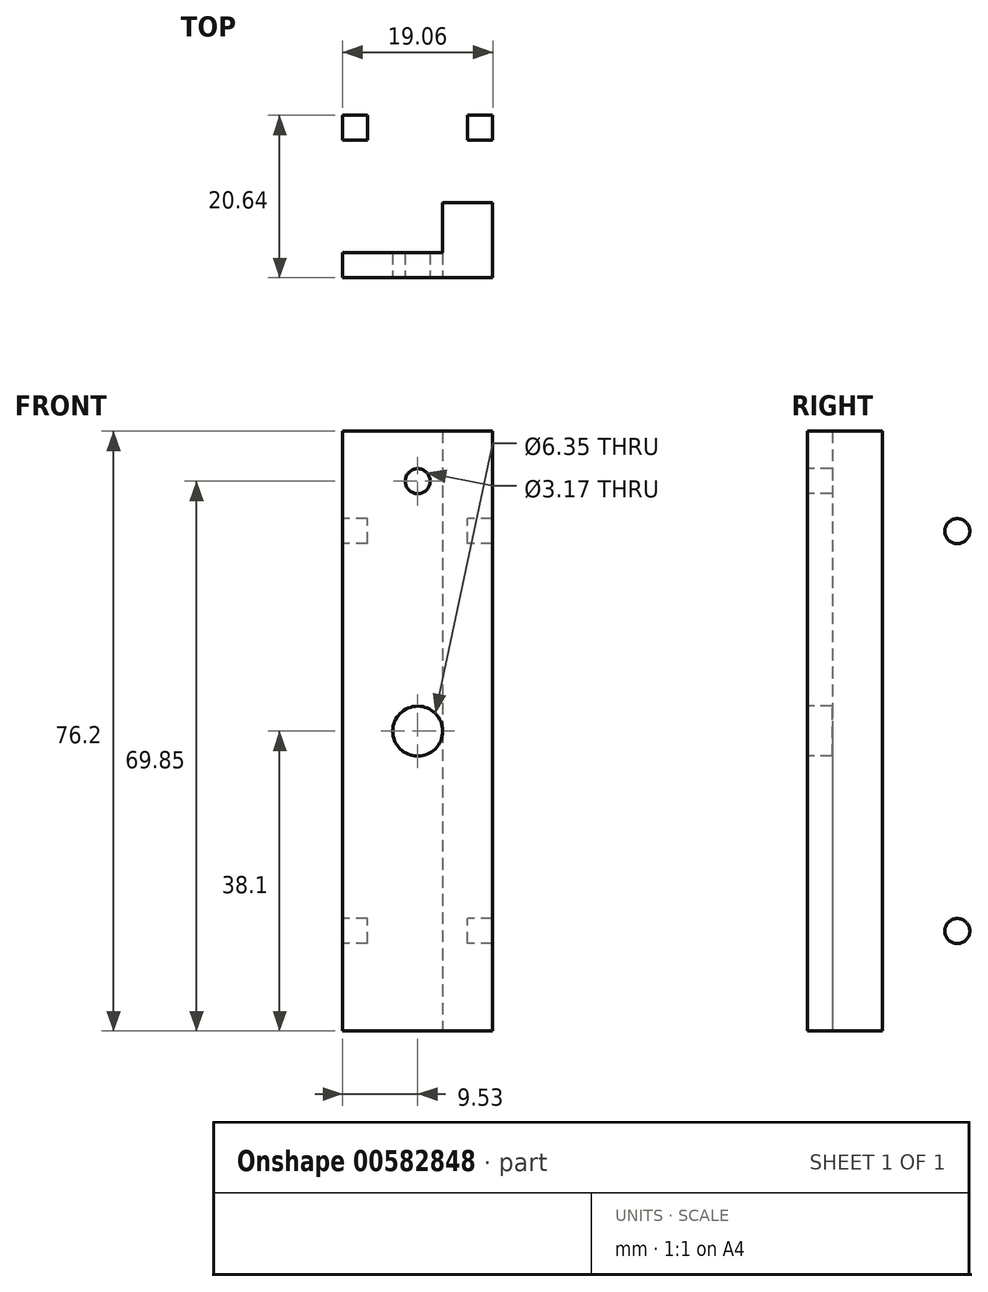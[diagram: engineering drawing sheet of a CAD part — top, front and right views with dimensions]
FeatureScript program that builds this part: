
annotation { "Feature Type Name" : "Feature", "Feature Type Description" : "" }
export const myFeature = defineFeature(function(context is Context, id is Id, definition is map)
    precondition{}
    {
        {
            var Q0;
            Q0=qCreatedBy(makeId("Front.planeOp"),FACE);
            var sketch = newSketch(context, id + "F0", { "sketchPlane" : qUnion([Q0])});
            skLineSegment(sketch, "E0.bottom", {"start": v(-9.53, -38.1) * mm, "end": v(9.53, -38.1) * mm});
            skLineSegment(sketch, "E0.top", {"start": v(-9.53, 38.1) * mm, "end": v(9.53, 38.1) * mm});
            skLineSegment(sketch, "E0.left", {"start": v(-9.53, -38.1) * mm, "end": v(-9.53, 38.1) * mm});
            skLineSegment(sketch, "E0.right", {"start": v(9.53, -38.1) * mm, "end": v(9.53, 38.1) * mm});
            skPoint(sketch, "E0.middle", {"position": v(0, 0) * mm});
            skSolve(sketch);
        }
        {
            var Q0;
            Q0 = qSketchRegion(id + "F0", true);
            extrude(context, id + "F1", {"entities" : qUnion([Q0]), "depth" : 22.22 * mm, "offsetDistance" : 25.4 * mm});
        }
        {
            var Q0;
            Q0=makeQuery(id+"F1.opExtrude","SWEPT_FACE",FACE,{"disambiguationData":[OSD([sQuery(id+"F0.wireOp",EDGE,"E0.left")])]});
            var sketch = newSketch(context, id + "F2", { "sketchPlane" : qUnion([Q0])});
            skLineSegment(sketch, "E1.bottom", {"start": v(12.7, 38.1) * mm, "end": v(19.05, 38.1) * mm});
            skLineSegment(sketch, "E1.top", {"start": v(12.7, -38.1) * mm, "end": v(19.05, -38.1) * mm});
            skLineSegment(sketch, "E1.left", {"start": v(12.7, 38.1) * mm, "end": v(12.7, -38.1) * mm});
            skLineSegment(sketch, "E1.right", {"start": v(19.05, 38.1) * mm, "end": v(19.05, -38.1) * mm});
            skSolve(sketch);
        }
        {
            var Q0;
            Q0=makeQuery(id+"F2.imprint","IMPRINT",FACE,{"disambiguationData":[TD([[makeQuery(id+"F2.imprint","IMPRINT",EDGE,{"derivedFrom":sQuery(id+"F2.wireOp",EDGE,"E1.bottom")}),1.0]])]});
            extrude(context, id + "F3", {"entities" : qUnion([Q0]), "operationType" : NewBodyOperationType.REMOVE, "oppositeDirection" : true, "depth" : 12.7 * mm, "offsetDistance" : 25.4 * mm});
        }
        {
            var Q0;
            Q0=makeQuery(id+"F1.opExtrude","CAP_FACE",FACE,{"disambiguationData":[OSD([sQuery(id+"F0.wireOp",EDGE,"E0.bottom"),sQuery(id+"F0.wireOp",EDGE,"E0.top"),sQuery(id+"F0.wireOp",EDGE,"E0.left"),sQuery(id+"F0.wireOp",EDGE,"E0.right")])],"isStart":true});
            var sketch = newSketch(context, id + "F4", { "sketchPlane" : qUnion([Q0])});
            skLineSegment(sketch, "E2.bottom", {"start": v(6.35, 38.1) * mm, "end": v(-6.35, 38.1) * mm});
            skLineSegment(sketch, "E2.top", {"start": v(6.35, -38.1) * mm, "end": v(-6.35, -38.1) * mm});
            skLineSegment(sketch, "E2.left", {"start": v(6.35, 38.1) * mm, "end": v(6.35, -38.1) * mm});
            skLineSegment(sketch, "E2.right", {"start": v(-6.35, 38.1) * mm, "end": v(-6.35, -38.1) * mm});
            skSolve(sketch);
        }
        {
            var Q0;
            Q0=makeQuery(id+"F4.imprint","IMPRINT",FACE,{"disambiguationData":[TD([[makeQuery(id+"F4.imprint","IMPRINT",EDGE,{"derivedFrom":sQuery(id+"F4.wireOp",EDGE,"E2.bottom")}),1.0]])]});
            extrude(context, id + "F5", {"entities" : qUnion([Q0]), "operationType" : NewBodyOperationType.REMOVE, "oppositeDirection" : true, "depth" : 9.52 * mm, "offsetDistance" : 25.4 * mm});
        }
        {
            var Q0;
            Q0=makeQuery(id+"F1.opExtrude","CAP_FACE",FACE,{"disambiguationData":[OSD([sQuery(id+"F0.wireOp",EDGE,"E0.bottom"),sQuery(id+"F0.wireOp",EDGE,"E0.top"),sQuery(id+"F0.wireOp",EDGE,"E0.left"),sQuery(id+"F0.wireOp",EDGE,"E0.right")])],"isStart":false});
            var sketch = newSketch(context, id + "F6", { "sketchPlane" : qUnion([Q0])});
            skCircle(sketch, "E3", {"center": v(0, 31.75) * mm, "radius": 1.59 * mm});
            skCircle(sketch, "E4", {"center": v(0, 0) * mm, "radius": 3.18 * mm});
            skSolve(sketch);
        }
        {
            var Q0;
            Q0=makeQuery(id+"F6.imprint","IMPRINT",FACE,{"disambiguationData":[TD([[makeQuery(id+"F6.imprint","IMPRINT",EDGE,{"derivedFrom":sQuery(id+"F6.wireOp",EDGE,"E3")}),1.0]])]});
            var Q1;
            Q1=makeQuery(id+"F6.imprint","IMPRINT",FACE,{"disambiguationData":[TD([[makeQuery(id+"F6.imprint","IMPRINT",EDGE,{"derivedFrom":sQuery(id+"F6.wireOp",EDGE,"E4")}),1.0]])]});
            extrude(context, id + "F7", {"entities" : qUnion([Q0, Q1]), "operationType" : NewBodyOperationType.REMOVE, "oppositeDirection" : true, "depth" : 19.05 * mm, "offsetDistance" : 25.4 * mm});
        }
        {
            var Q0;
            {var subQ1=sQuery(id+"F0.wireOp",EDGE,"E0.left");Q0=makeQuery(id+"F3.boolean.opBoolean","SPLIT",FACE,{"disambiguationData":[TD([makeQuery(id+"F3.opExtrude","SWEPT_FACE",FACE,{"disambiguationData":[OSD([sQuery(id+"F2.wireOp",EDGE,"E1.left")])]})])],"derivedFrom":makeQuery(id+"F1.opExtrude","SWEPT_FACE",FACE,{"disambiguationData":[OSD([subQ1])]})});}
            var sketch = newSketch(context, id + "F8", { "sketchPlane" : qUnion([Q0])});
            skLineSegment(sketch, "E5", {"start": v(0, 38.1) * mm, "end": v(3.17, 38.1) * mm});
            skLineSegment(sketch, "E6", {"start": v(3.17, 38.1) * mm, "end": v(3.18, -38.1) * mm});
            skCircle(sketch, "E7", {"center": v(3.17, 25.4) * mm, "radius": 1.59 * mm});
            skCircle(sketch, "E8", {"center": v(3.18, -25.4) * mm, "radius": 1.59 * mm});
            skSolve(sketch);
        }
        {
            var Q0;
            {var subQ0=sQuery(id+"F8.wireOp",EDGE,"E7");var subQ1=sQuery(id+"F8.wireOp",EDGE,"E6");var subQ2=makeQuery(id+"F8.imprint","INTERSECT",VERTEX,{"disambiguationData":[OD(0.0)],"derivedFrom":[subQ1,subQ0]});Q0=makeQuery(id+"F8.imprint","IMPRINT",FACE,{"disambiguationData":[TD([[makeQuery(id+"F8.imprint","IMPRINT",EDGE,{"disambiguationData":[TD([[subQ2,-1.0]])],"derivedFrom":subQ1}),-1.0]])]});}
            var Q1;
            {var subQ0=sQuery(id+"F8.wireOp",EDGE,"E7");var subQ1=sQuery(id+"F8.wireOp",EDGE,"E6");var subQ2=makeQuery(id+"F8.imprint","INTERSECT",VERTEX,{"disambiguationData":[OD(0.0)],"derivedFrom":[subQ1,subQ0]});Q1=makeQuery(id+"F8.imprint","IMPRINT",FACE,{"disambiguationData":[TD([[makeQuery(id+"F8.imprint","IMPRINT",EDGE,{"disambiguationData":[TD([[subQ2,-1.0]])],"derivedFrom":subQ1}),1.0]])]});}
            var Q2;
            {var subQ0=sQuery(id+"F8.wireOp",EDGE,"E8");var subQ1=sQuery(id+"F8.wireOp",EDGE,"E6");var subQ2=makeQuery(id+"F8.imprint","INTERSECT",VERTEX,{"disambiguationData":[OD(0.0)],"derivedFrom":[subQ1,subQ0]});Q2=makeQuery(id+"F8.imprint","IMPRINT",FACE,{"disambiguationData":[TD([[makeQuery(id+"F8.imprint","IMPRINT",EDGE,{"disambiguationData":[TD([[subQ2,-1.0]])],"derivedFrom":subQ1}),-1.0]])]});}
            var Q3;
            {var subQ0=sQuery(id+"F8.wireOp",EDGE,"E8");var subQ1=sQuery(id+"F8.wireOp",EDGE,"E6");var subQ2=makeQuery(id+"F8.imprint","INTERSECT",VERTEX,{"disambiguationData":[OD(0.0)],"derivedFrom":[subQ1,subQ0]});Q3=makeQuery(id+"F8.imprint","IMPRINT",FACE,{"disambiguationData":[TD([[makeQuery(id+"F8.imprint","IMPRINT",EDGE,{"disambiguationData":[TD([[subQ2,-1.0]])],"derivedFrom":subQ1}),1.0]])]});}
            extrude(context, id + "F9", {"entities" : qUnion([Q0, Q1, Q2, Q3]), "operationType" : NewBodyOperationType.REMOVE, "oppositeDirection" : true, "depth" : 25.4 * mm, "offsetDistance" : 25.4 * mm});
        }
    });
